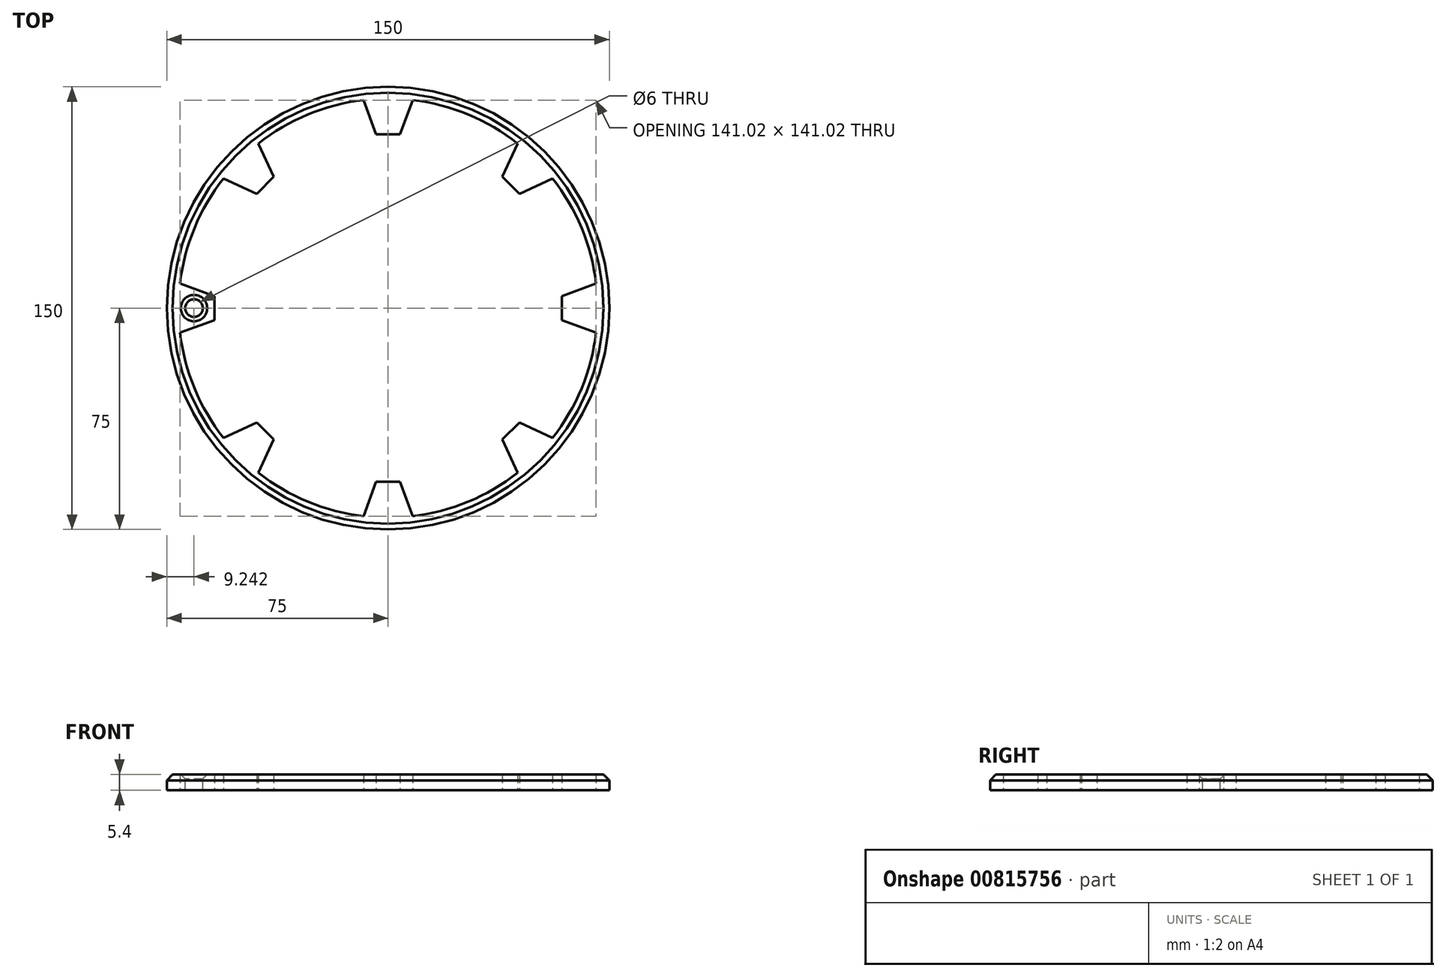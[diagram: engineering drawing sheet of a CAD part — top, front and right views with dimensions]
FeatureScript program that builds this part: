
annotation { "Feature Type Name" : "Feature", "Feature Type Description" : "" }
export const myFeature = defineFeature(function(context is Context, id is Id, definition is map)
    precondition{}
    {
        {
            var Q0;
            Q0=qCreatedBy(makeId("Top.planeOp"),FACE);
            var sketch = newSketch(context, id + "F0", { "sketchPlane" : qUnion([Q0])});
            skLineSegment(sketch, "E0.0", {"start": v(-69.42, -9) * mm, "end": v(-57.86, -4.8) * mm});
            skArc(sketch, "E1.0", {"start": v(-69.42, -9) * mm, "mid": v(-64.67, -26.79) * mm, "end": v(-55.45, -42.72) * mm});
            skLineSegment(sketch, "E2.0", {"start": v(-69.42, 9) * mm, "end": v(-57.86, 4.8) * mm});
            skArc(sketch, "E3.0", {"start": v(-55.45, 42.72) * mm, "mid": v(-64.67, 26.79) * mm, "end": v(-69.42, 9) * mm});
            skLineSegment(sketch, "E4.0", {"start": v(-55.45, 42.72) * mm, "end": v(-44.3, 37.52) * mm});
            skLineSegment(sketch, "E5.0", {"start": v(-44.3, 37.52) * mm, "end": v(-37.52, 44.3) * mm});
            skLineSegment(sketch, "E6.0", {"start": v(-42.72, 55.45) * mm, "end": v(-37.52, 44.3) * mm});
            skArc(sketch, "E7.0", {"start": v(-9, 69.42) * mm, "mid": v(-26.79, 64.67) * mm, "end": v(-42.72, 55.45) * mm});
            skLineSegment(sketch, "E8.0", {"start": v(-9, 69.42) * mm, "end": v(-4.8, 57.86) * mm});
            skLineSegment(sketch, "E9.0", {"start": v(-4.8, 57.86) * mm, "end": v(4.8, 57.86) * mm});
            skLineSegment(sketch, "E10.0", {"start": v(9, 69.42) * mm, "end": v(4.8, 57.86) * mm});
            skArc(sketch, "E11.0", {"start": v(42.72, 55.45) * mm, "mid": v(26.79, 64.67) * mm, "end": v(9, 69.42) * mm});
            skLineSegment(sketch, "E12.0", {"start": v(42.72, 55.45) * mm, "end": v(37.52, 44.3) * mm});
            skLineSegment(sketch, "E13.0", {"start": v(37.52, 44.3) * mm, "end": v(44.3, 37.52) * mm});
            skLineSegment(sketch, "E14.0", {"start": v(55.45, 42.72) * mm, "end": v(44.3, 37.52) * mm});
            skArc(sketch, "E15.0", {"start": v(69.42, 9) * mm, "mid": v(64.67, 26.79) * mm, "end": v(55.45, 42.72) * mm});
            skLineSegment(sketch, "E16.0", {"start": v(69.42, 9) * mm, "end": v(57.86, 4.8) * mm});
            skLineSegment(sketch, "E17.0", {"start": v(57.86, 4.8) * mm, "end": v(57.86, -4.8) * mm});
            skLineSegment(sketch, "E18.0", {"start": v(69.42, -9) * mm, "end": v(57.86, -4.8) * mm});
            skArc(sketch, "E19.0", {"start": v(55.45, -42.72) * mm, "mid": v(64.67, -26.79) * mm, "end": v(69.42, -9) * mm});
            skLineSegment(sketch, "E20.0", {"start": v(55.45, -42.72) * mm, "end": v(44.3, -37.52) * mm});
            skLineSegment(sketch, "E21.0", {"start": v(44.3, -37.52) * mm, "end": v(37.52, -44.3) * mm});
            skArc(sketch, "E22.0", {"start": v(9, -69.42) * mm, "mid": v(26.79, -64.67) * mm, "end": v(42.72, -55.45) * mm});
            skLineSegment(sketch, "E23.0", {"start": v(42.72, -55.45) * mm, "end": v(37.52, -44.3) * mm});
            skLineSegment(sketch, "E24.0", {"start": v(9, -69.42) * mm, "end": v(4.8, -57.86) * mm});
            skLineSegment(sketch, "E25.0", {"start": v(4.8, -57.86) * mm, "end": v(-4.8, -57.86) * mm});
            skLineSegment(sketch, "E26.0", {"start": v(-9, -69.42) * mm, "end": v(-4.8, -57.86) * mm});
            skArc(sketch, "E27.0", {"start": v(-42.72, -55.45) * mm, "mid": v(-26.79, -64.67) * mm, "end": v(-9, -69.42) * mm});
            skLineSegment(sketch, "E28.0", {"start": v(-42.72, -55.45) * mm, "end": v(-37.52, -44.3) * mm});
            skLineSegment(sketch, "E29.0", {"start": v(-37.52, -44.3) * mm, "end": v(-44.3, -37.52) * mm});
            skLineSegment(sketch, "E30.0", {"start": v(-55.45, -42.72) * mm, "end": v(-44.3, -37.52) * mm});
            skCircle(sketch, "E31.0", {"center": v(0, 0) * mm, "radius": 75 * mm});
            skLineSegment(sketch, "E32", {"start": v(-57.86, 4.8) * mm, "end": v(-57.86, -4.8) * mm});
            skLineSegment(sketch, "E33.0", {"start": v(-55.75, 43.97) * mm, "end": v(-44.51, 38.73) * mm});
            skLineSegment(sketch, "E33.1", {"start": v(-44.51, 38.73) * mm, "end": v(-38.73, 44.51) * mm});
            skLineSegment(sketch, "E33.2", {"start": v(-43.97, 55.75) * mm, "end": v(-38.73, 44.51) * mm});
            skArc(sketch, "E33.3", {"start": v(-8.33, 70.5) * mm, "mid": v(-27.17, 65.6) * mm, "end": v(-43.97, 55.75) * mm});
            skLineSegment(sketch, "E33.4", {"start": v(-8.33, 70.5) * mm, "end": v(-4.1, 58.86) * mm});
            skLineSegment(sketch, "E33.5", {"start": v(-4.1, 58.86) * mm, "end": v(4.1, 58.86) * mm});
            skLineSegment(sketch, "E33.6", {"start": v(8.33, 70.5) * mm, "end": v(4.1, 58.86) * mm});
            skArc(sketch, "E33.7", {"start": v(43.97, 55.75) * mm, "mid": v(27.17, 65.6) * mm, "end": v(8.33, 70.5) * mm});
            skLineSegment(sketch, "E33.8", {"start": v(43.97, 55.75) * mm, "end": v(38.73, 44.51) * mm});
            skLineSegment(sketch, "E33.9", {"start": v(4.1, -58.86) * mm, "end": v(-4.1, -58.86) * mm});
            skLineSegment(sketch, "E33.10", {"start": v(-8.33, -70.5) * mm, "end": v(-4.1, -58.86) * mm});
            skArc(sketch, "E33.11", {"start": v(-43.97, -55.75) * mm, "mid": v(-27.17, -65.6) * mm, "end": v(-8.33, -70.5) * mm});
            skLineSegment(sketch, "E33.12", {"start": v(-43.97, -55.75) * mm, "end": v(-38.73, -44.51) * mm});
            skLineSegment(sketch, "E33.13", {"start": v(-38.73, -44.51) * mm, "end": v(-44.51, -38.73) * mm});
            skLineSegment(sketch, "E33.14", {"start": v(-55.75, -43.97) * mm, "end": v(-44.51, -38.73) * mm});
            skLineSegment(sketch, "E33.15", {"start": v(-70.5, 8.33) * mm, "end": v(-58.86, 4.1) * mm});
            skLineSegment(sketch, "E33.16", {"start": v(-58.86, 4.1) * mm, "end": v(-58.86, -4.1) * mm});
            skLineSegment(sketch, "E33.17", {"start": v(-70.5, -8.33) * mm, "end": v(-58.86, -4.1) * mm});
            skArc(sketch, "E33.18", {"start": v(-70.5, -8.33) * mm, "mid": v(-65.6, -27.17) * mm, "end": v(-55.75, -43.97) * mm});
            skLineSegment(sketch, "E33.19", {"start": v(8.33, -70.5) * mm, "end": v(4.1, -58.86) * mm});
            skArc(sketch, "E33.20", {"start": v(8.33, -70.5) * mm, "mid": v(27.17, -65.6) * mm, "end": v(43.97, -55.75) * mm});
            skLineSegment(sketch, "E33.21", {"start": v(43.97, -55.75) * mm, "end": v(38.73, -44.51) * mm});
            skLineSegment(sketch, "E33.22", {"start": v(44.51, -38.73) * mm, "end": v(38.73, -44.51) * mm});
            skLineSegment(sketch, "E33.23", {"start": v(55.75, -43.97) * mm, "end": v(44.51, -38.73) * mm});
            skArc(sketch, "E33.24", {"start": v(55.75, -43.97) * mm, "mid": v(65.6, -27.17) * mm, "end": v(70.5, -8.33) * mm});
            skLineSegment(sketch, "E33.25", {"start": v(70.5, -8.33) * mm, "end": v(58.86, -4.1) * mm});
            skLineSegment(sketch, "E33.26", {"start": v(58.86, 4.1) * mm, "end": v(58.86, -4.1) * mm});
            skLineSegment(sketch, "E33.27", {"start": v(70.5, 8.33) * mm, "end": v(58.86, 4.1) * mm});
            skArc(sketch, "E33.28", {"start": v(-55.75, 43.97) * mm, "mid": v(-65.6, 27.17) * mm, "end": v(-70.5, 8.33) * mm});
            skArc(sketch, "E33.29", {"start": v(70.5, 8.33) * mm, "mid": v(65.6, 27.17) * mm, "end": v(55.75, 43.97) * mm});
            skLineSegment(sketch, "E33.30", {"start": v(55.75, 43.97) * mm, "end": v(44.51, 38.73) * mm});
            skLineSegment(sketch, "E33.31", {"start": v(38.73, 44.51) * mm, "end": v(44.51, 38.73) * mm});
            skSolve(sketch);
        }
        {
            var Q0;
            Q0=makeQuery(id+"F0.imprint","IMPRINT",FACE,{"disambiguationData":[TD([[makeQuery(id+"F0.imprint","IMPRINT",EDGE,{"derivedFrom":sQuery(id+"F0.wireOp",EDGE,"E31.0")}),1.0]])]});
            extrude(context, id + "F1", {"entities" : qUnion([Q0]), "depth" : 5.4 * mm, "offsetDistance" : 25 * mm});
        }
        {
            var Q0;
            Q0=makeQuery(id+"F1.opExtrude","CAP_FACE",FACE,{"disambiguationData":[OSD([sQuery(id+"F0.wireOp",EDGE,"E31.0"),sQuery(id+"F0.wireOp",EDGE,"E33.0"),sQuery(id+"F0.wireOp",EDGE,"E33.1"),sQuery(id+"F0.wireOp",EDGE,"E33.2"),sQuery(id+"F0.wireOp",EDGE,"E33.3"),sQuery(id+"F0.wireOp",EDGE,"E33.4"),sQuery(id+"F0.wireOp",EDGE,"E33.5"),sQuery(id+"F0.wireOp",EDGE,"E33.6"),sQuery(id+"F0.wireOp",EDGE,"E33.7"),sQuery(id+"F0.wireOp",EDGE,"E33.8"),sQuery(id+"F0.wireOp",EDGE,"E33.9"),sQuery(id+"F0.wireOp",EDGE,"E33.10"),sQuery(id+"F0.wireOp",EDGE,"E33.11"),sQuery(id+"F0.wireOp",EDGE,"E33.12"),sQuery(id+"F0.wireOp",EDGE,"E33.13"),sQuery(id+"F0.wireOp",EDGE,"E33.14"),sQuery(id+"F0.wireOp",EDGE,"E33.15"),sQuery(id+"F0.wireOp",EDGE,"E33.16"),sQuery(id+"F0.wireOp",EDGE,"E33.17"),sQuery(id+"F0.wireOp",EDGE,"E33.18"),sQuery(id+"F0.wireOp",EDGE,"E33.19"),sQuery(id+"F0.wireOp",EDGE,"E33.20"),sQuery(id+"F0.wireOp",EDGE,"E33.21"),sQuery(id+"F0.wireOp",EDGE,"E33.22"),sQuery(id+"F0.wireOp",EDGE,"E33.23"),sQuery(id+"F0.wireOp",EDGE,"E33.24"),sQuery(id+"F0.wireOp",EDGE,"E33.25"),sQuery(id+"F0.wireOp",EDGE,"E33.26"),sQuery(id+"F0.wireOp",EDGE,"E33.27"),sQuery(id+"F0.wireOp",EDGE,"E33.28"),sQuery(id+"F0.wireOp",EDGE,"E33.29"),sQuery(id+"F0.wireOp",EDGE,"E33.30"),sQuery(id+"F0.wireOp",EDGE,"E33.31")])],"isStart":false});
            var sketch = newSketch(context, id + "F2", { "sketchPlane" : qUnion([Q0])});
            skLineSegment(sketch, "E34", {"start": v(0, 0) * mm, "end": v(-102.44, 0) * mm, "construction": true});
            skPoint(sketch, "E35", {"position": v(-65.76, 0) * mm});
            skPoint(sketch, "E36", {"position": v(-75, 0) * mm});
            skSolve(sketch);
        }
        {
            var Q0;
            Q0=sQuery(id+"F2.wireOp",VERTEX,"E35");
            var Q1;
            Q1=makeQuery(id+"F1.opExtrude","SWEPT_BODY",BODY,{"disambiguationData":[OSD([sQuery(id+"F0.wireOp",EDGE,"E31.0"),sQuery(id+"F0.wireOp",EDGE,"E33.0"),sQuery(id+"F0.wireOp",EDGE,"E33.1"),sQuery(id+"F0.wireOp",EDGE,"E33.2"),sQuery(id+"F0.wireOp",EDGE,"E33.3"),sQuery(id+"F0.wireOp",EDGE,"E33.4"),sQuery(id+"F0.wireOp",EDGE,"E33.5"),sQuery(id+"F0.wireOp",EDGE,"E33.6"),sQuery(id+"F0.wireOp",EDGE,"E33.7"),sQuery(id+"F0.wireOp",EDGE,"E33.8"),sQuery(id+"F0.wireOp",EDGE,"E33.9"),sQuery(id+"F0.wireOp",EDGE,"E33.10"),sQuery(id+"F0.wireOp",EDGE,"E33.11"),sQuery(id+"F0.wireOp",EDGE,"E33.12"),sQuery(id+"F0.wireOp",EDGE,"E33.13"),sQuery(id+"F0.wireOp",EDGE,"E33.14"),sQuery(id+"F0.wireOp",EDGE,"E33.15"),sQuery(id+"F0.wireOp",EDGE,"E33.16"),sQuery(id+"F0.wireOp",EDGE,"E33.17"),sQuery(id+"F0.wireOp",EDGE,"E33.18"),sQuery(id+"F0.wireOp",EDGE,"E33.19"),sQuery(id+"F0.wireOp",EDGE,"E33.20"),sQuery(id+"F0.wireOp",EDGE,"E33.21"),sQuery(id+"F0.wireOp",EDGE,"E33.22"),sQuery(id+"F0.wireOp",EDGE,"E33.23"),sQuery(id+"F0.wireOp",EDGE,"E33.24"),sQuery(id+"F0.wireOp",EDGE,"E33.25"),sQuery(id+"F0.wireOp",EDGE,"E33.26"),sQuery(id+"F0.wireOp",EDGE,"E33.27"),sQuery(id+"F0.wireOp",EDGE,"E33.28"),sQuery(id+"F0.wireOp",EDGE,"E33.29"),sQuery(id+"F0.wireOp",EDGE,"E33.30"),sQuery(id+"F0.wireOp",EDGE,"E33.31")])]});
            hole(context, id + "F3", {"style" : HoleStyle.C_SINK, "endStyle" : HoleEndStyle.BLIND, "holeDiameter" : 6 * mm, "cSinkDiameter" : 8.96 * mm, "cSinkAngle" : 90 * degree, "majorDiameter" : 5 * mm, "holeDepth" : 6 * mm, "isTappedThrough" : true, "tappedDepth" : 12 * mm, "tapClearance" : 3, "startFromSketch" : true, "locations" : qUnion([Q0]), "scope" : qUnion([Q1])});
        }
        {
            var Q0;
            Q0=makeQuery(id+"F1.opExtrude","CAP_EDGE",EDGE,{"disambiguationData":[OSD([sQuery(id+"F0.wireOp",EDGE,"E31.0")])],"isStart":false});
            chamfer(context, id + "F4", {"entities" : qUnion([Q0]), "width" : 2 * mm, "tangentPropagation" : true});
        }
    });
